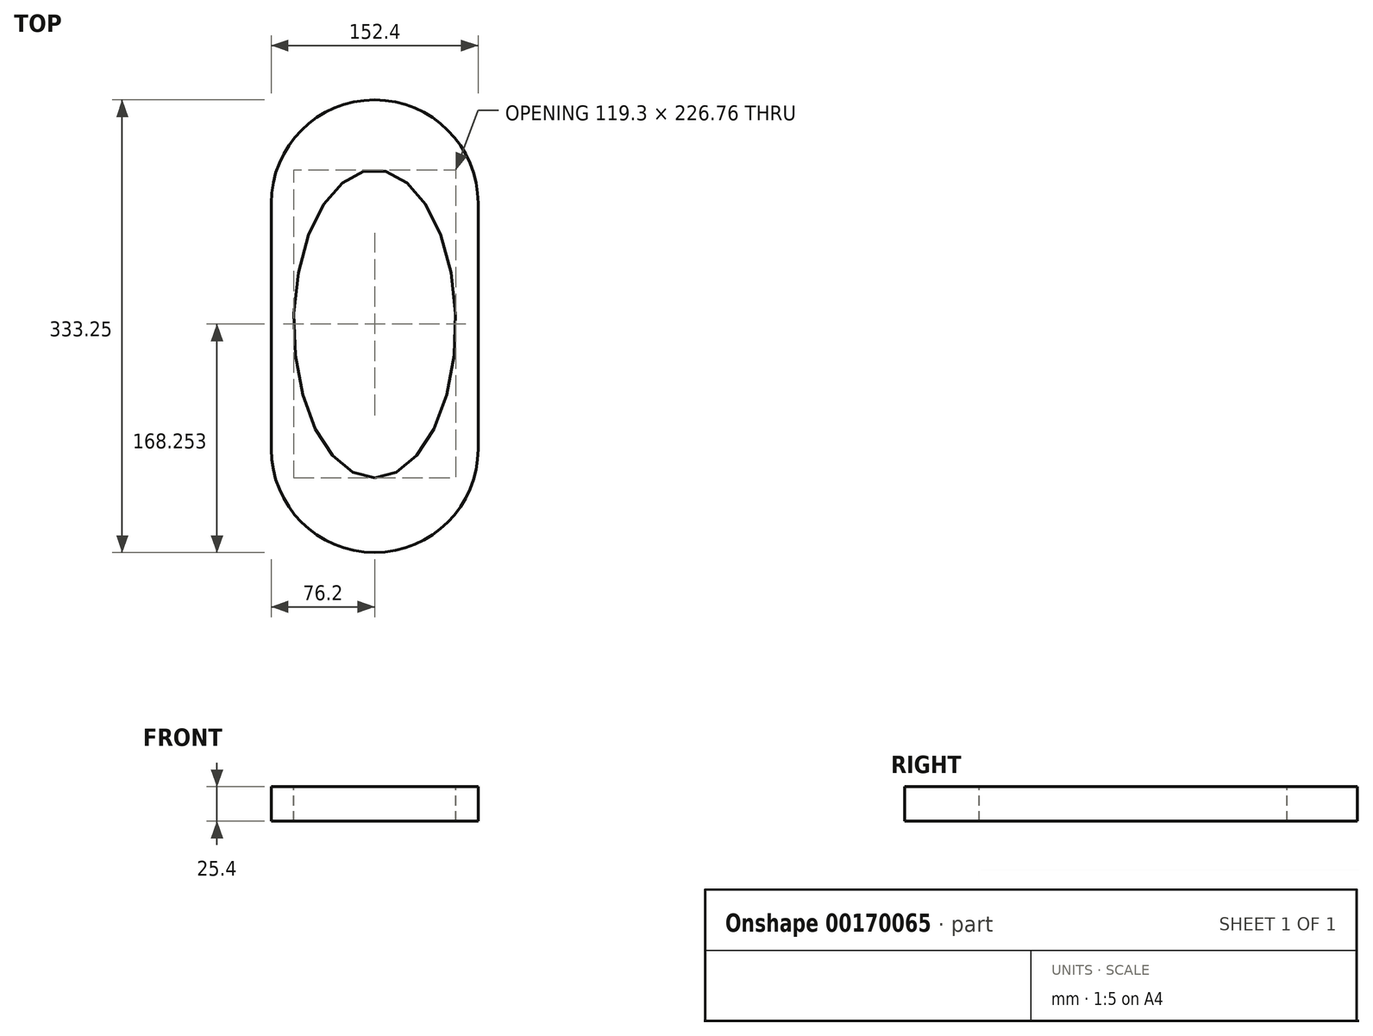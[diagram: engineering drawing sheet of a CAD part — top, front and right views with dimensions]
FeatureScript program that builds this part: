
annotation { "Feature Type Name" : "Feature", "Feature Type Description" : "" }
export const myFeature = defineFeature(function(context is Context, id is Id, definition is map)
    precondition{}
    {
        {
            var Q0;
            Q0=qCreatedBy(makeId("Top.planeOp"),FACE);
            var sketch = newSketch(context, id + "F0", { "sketchPlane" : qUnion([Q0])});
            skArc(sketch, "E0", {"start": v(76.2, 0) * mm, "mid": v(0, 76.2) * mm, "end": v(-76.2, 0) * mm});
            skLineSegment(sketch, "E1", {"start": v(-76.2, 0) * mm, "end": v(76.2, 0) * mm});
            skLineSegment(sketch, "E2.top", {"start": v(-76.2, -180.85) * mm, "end": v(76.2, -180.85) * mm});
            skLineSegment(sketch, "E2.left", {"start": v(-76.2, 0) * mm, "end": v(-76.2, -180.85) * mm});
            skLineSegment(sketch, "E2.right", {"start": v(76.2, 0) * mm, "end": v(76.2, -180.85) * mm});
            skArc(sketch, "E3", {"start": v(-76.2, -180.85) * mm, "mid": v(0, -257.05) * mm, "end": v(76.2, -180.85) * mm});
            skSolve(sketch);
        }
        {
            var Q0;
            Q0=makeQuery(id+"F0.imprint","IMPRINT",FACE,{"disambiguationData":[TD([[makeQuery(id+"F0.imprint","IMPRINT",EDGE,{"derivedFrom":sQuery(id+"F0.wireOp",EDGE,"E1")}),-1.0]])]});
            var Q1;
            Q1=makeQuery(id+"F0.imprint","IMPRINT",FACE,{"disambiguationData":[TD([[makeQuery(id+"F0.imprint","IMPRINT",EDGE,{"derivedFrom":sQuery(id+"F0.wireOp",EDGE,"E0")}),1.0]])]});
            var Q2;
            Q2=makeQuery(id+"F0.imprint","IMPRINT",FACE,{"disambiguationData":[TD([[makeQuery(id+"F0.imprint","IMPRINT",EDGE,{"derivedFrom":sQuery(id+"F0.wireOp",EDGE,"E2.top")}),-1.0]])]});
            extrude(context, id + "F1", {"entities" : qUnion([Q0, Q1, Q2]), "depth" : 25.4 * mm});
        }
        {
            var Q0;
            Q0=makeQuery(id+"F1.opExtrude","CAP_FACE",FACE,{"disambiguationData":[OSD([sQuery(id+"F0.wireOp",EDGE,"E0"),sQuery(id+"F0.wireOp",EDGE,"E2.left"),sQuery(id+"F0.wireOp",EDGE,"E2.right"),sQuery(id+"F0.wireOp",EDGE,"E3")])],"isStart":false});
            var sketch = newSketch(context, id + "F2", { "sketchPlane" : qUnion([Q0])});
            skEllipse(sketch, "E4", {"center": v(0, -88.8) * mm, "majorRadius": 113.38 * mm, "minorRadius": 59.65 * mm, "majorAxis": v(0, -1)});
            skSolve(sketch);
        }
        {
            var Q0;
            Q0=makeQuery(id+"F2.imprint","IMPRINT",FACE,{"disambiguationData":[TD([[makeQuery(id+"F2.imprint","IMPRINT",EDGE,{"derivedFrom":sQuery(id+"F2.wireOp",EDGE,"E4")}),1.0]])]});
            extrude(context, id + "F3", {"entities" : qUnion([Q0]), "operationType" : NewBodyOperationType.REMOVE, "oppositeDirection" : true, "depth" : 25.4 * mm});
        }
    });
